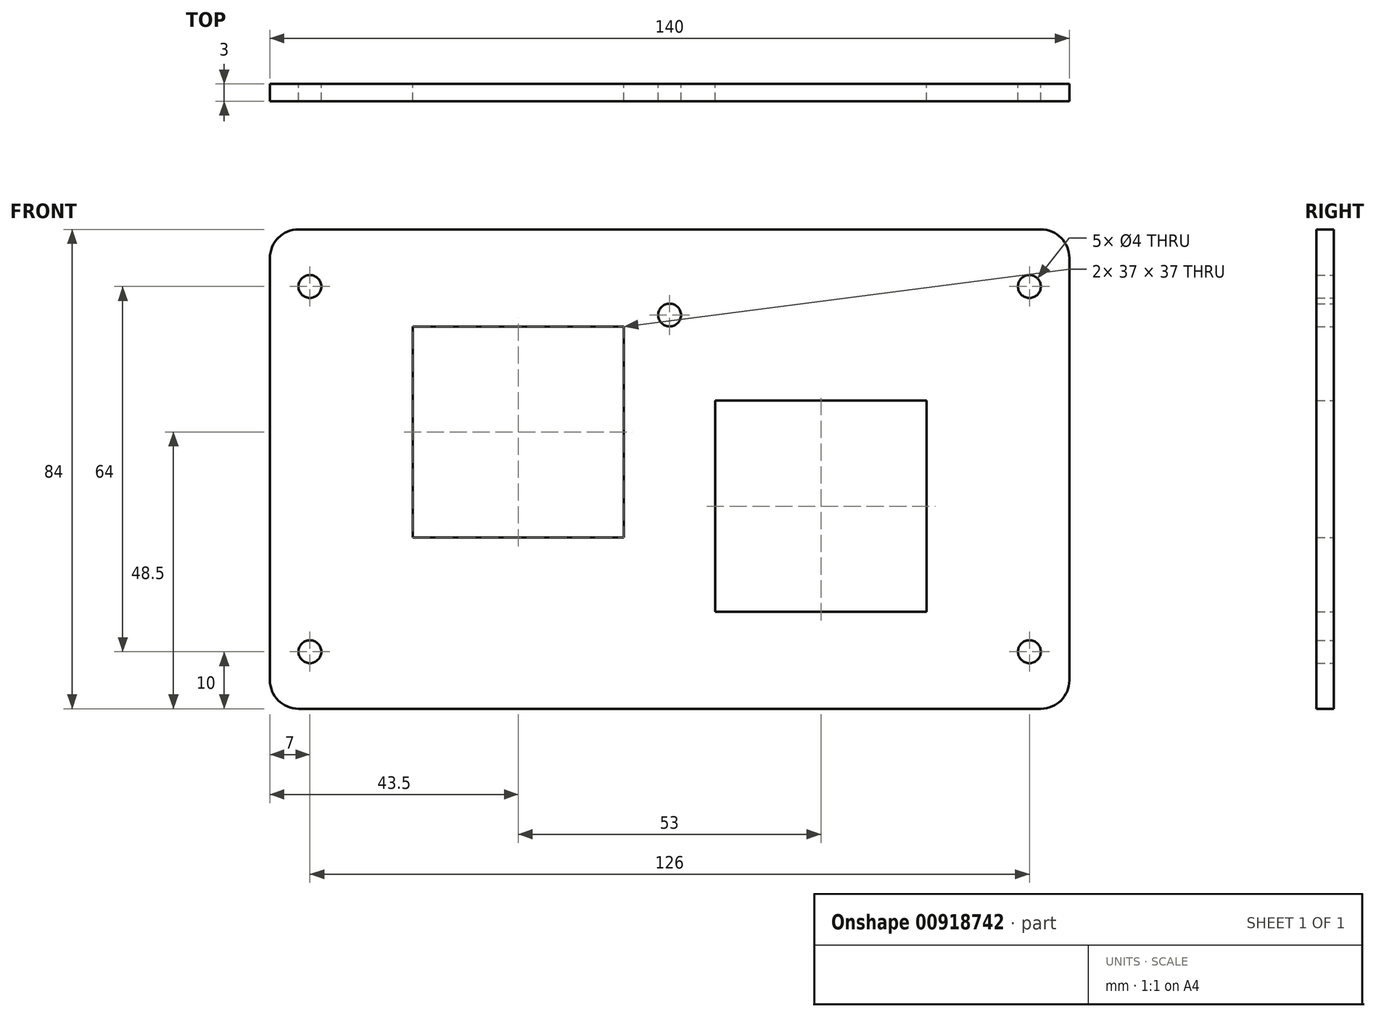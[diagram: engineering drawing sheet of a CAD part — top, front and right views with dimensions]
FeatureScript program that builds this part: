
annotation { "Feature Type Name" : "Feature", "Feature Type Description" : "" }
export const myFeature = defineFeature(function(context is Context, id is Id, definition is map)
    precondition{}
    {
        {
            var Q0;
            Q0=qCreatedBy(makeId("Front.planeOp"),FACE);
            var sketch = newSketch(context, id + "F0", { "sketchPlane" : qUnion([Q0])});
            skLineSegment(sketch, "E0.bottom", {"start": v(-65, 42) * mm, "end": v(65, 42) * mm});
            skLineSegment(sketch, "E0.top", {"start": v(-65, -42) * mm, "end": v(65, -42) * mm});
            skLineSegment(sketch, "E0.left", {"start": v(-70, 37) * mm, "end": v(-70, -37) * mm});
            skLineSegment(sketch, "E0.right", {"start": v(70, 37) * mm, "end": v(70, -37) * mm});
            skPoint(sketch, "E0.middle", {"position": v(0, 0) * mm});
            skLineSegment(sketch, "E1", {"start": v(-70, 32) * mm, "end": v(70, 32) * mm, "construction": true});
            skLineSegment(sketch, "E2.MirrorCS", {"start": v(-70, -32) * mm, "end": v(70, -32) * mm, "construction": true});
            skLineSegment(sketch, "E3", {"start": v(-63, 42) * mm, "end": v(-63, -42) * mm, "construction": true});
            skLineSegment(sketch, "E4.MirrorCS", {"start": v(63, 42) * mm, "end": v(63, -42) * mm, "construction": true});
            skCircle(sketch, "E5", {"center": v(0, 27) * mm, "radius": 2 * mm});
            skCircle(sketch, "E6", {"center": v(-63, 32) * mm, "radius": 2 * mm});
            skCircle(sketch, "E7.MirrorC", {"center": v(63, 32) * mm, "radius": 2 * mm});
            skCircle(sketch, "E8.MirrorC", {"center": v(-63, -32) * mm, "radius": 2 * mm});
            skCircle(sketch, "E9.MirrorC", {"center": v(63, -32) * mm, "radius": 2 * mm});
            skPoint(sketch, "E10.visualSharp", {"position": v(-70, 42) * mm});
            skArc(sketch, "E10.filletArc", {"start": v(-65, 42) * mm, "mid": v(-68.54, 40.54) * mm, "end": v(-70, 37) * mm});
            skPoint(sketch, "E11.visualSharp", {"position": v(70, 42) * mm});
            skArc(sketch, "E11.filletArc", {"start": v(70, 37) * mm, "mid": v(68.54, 40.54) * mm, "end": v(65, 42) * mm});
            skPoint(sketch, "E12.visualSharp", {"position": v(70, -42) * mm});
            skArc(sketch, "E12.filletArc", {"start": v(65, -42) * mm, "mid": v(68.54, -40.54) * mm, "end": v(70, -37) * mm});
            skPoint(sketch, "E13.visualSharp", {"position": v(-70, -42) * mm});
            skArc(sketch, "E13.filletArc", {"start": v(-70, -37) * mm, "mid": v(-68.54, -40.54) * mm, "end": v(-65, -42) * mm});
            skLineSegment(sketch, "E14.bottom", {"start": v(-45, 25) * mm, "end": v(-8, 25) * mm});
            skLineSegment(sketch, "E14.top", {"start": v(-45, -12) * mm, "end": v(-8, -12) * mm});
            skLineSegment(sketch, "E14.left", {"start": v(-45, 25) * mm, "end": v(-45, -12) * mm});
            skLineSegment(sketch, "E14.right", {"start": v(-8, 25) * mm, "end": v(-8, -12) * mm});
            skLineSegment(sketch, "E15.bottom", {"start": v(8, 12) * mm, "end": v(45, 12) * mm});
            skLineSegment(sketch, "E15.top", {"start": v(8, -25) * mm, "end": v(45, -25) * mm});
            skLineSegment(sketch, "E15.left", {"start": v(8, 12) * mm, "end": v(8, -25) * mm});
            skLineSegment(sketch, "E15.right", {"start": v(45, 12) * mm, "end": v(45, -25) * mm});
            skSolve(sketch);
        }
        {
            var Q0;
            Q0=makeQuery(id+"F0.imprint","IMPRINT",FACE,{"disambiguationData":[TD([[makeQuery(id+"F0.imprint","IMPRINT",EDGE,{"derivedFrom":sQuery(id+"F0.wireOp",EDGE,"E0.bottom")}),-1.0]])]});
            extrude(context, id + "F1", {"entities" : qUnion([Q0]), "depth" : 3 * mm, "offsetDistance" : 25 * mm});
        }
    });
